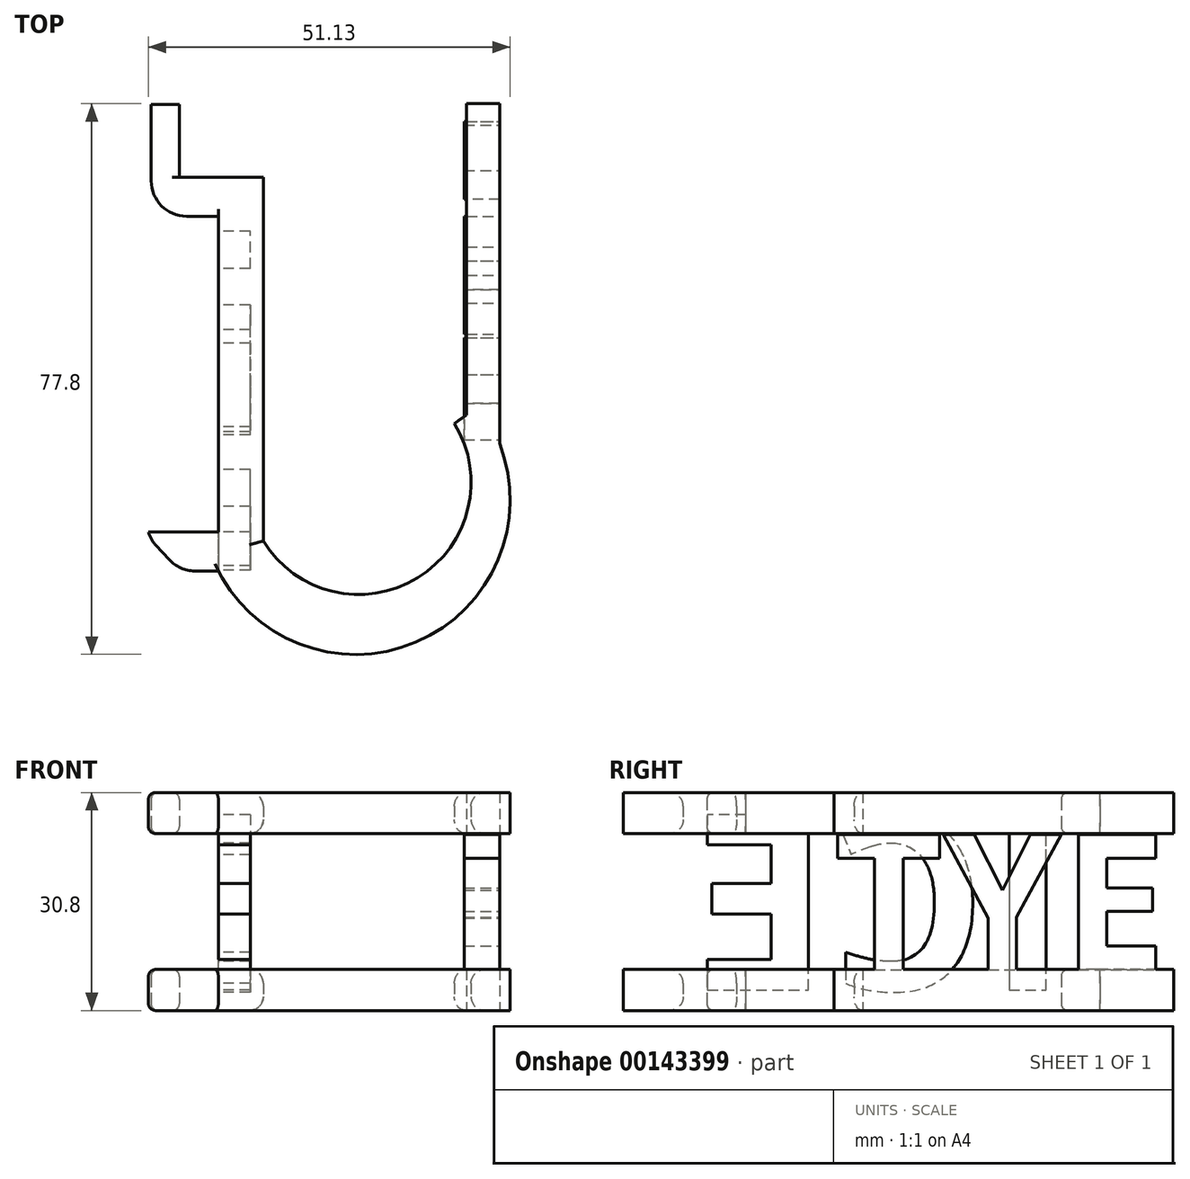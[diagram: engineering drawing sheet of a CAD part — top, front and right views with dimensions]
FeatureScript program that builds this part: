
annotation { "Feature Type Name" : "Feature", "Feature Type Description" : "" }
export const myFeature = defineFeature(function(context is Context, id is Id, definition is map)
    precondition{}
    {
        {
            var Q0;
            Q0=qCreatedBy(makeId("Top.planeOp"),FACE);
            var sketch = newSketch(context, id + "F0", { "sketchPlane" : qUnion([Q0])});
            skLineSegment(sketch, "E0.top", {"start": v(0, 55.6) * mm, "end": v(6.35, 55.6) * mm});
            skLineSegment(sketch, "E0.left", {"start": v(0, 0) * mm, "end": v(0, 55.6) * mm});
            skLineSegment(sketch, "E0.right", {"start": v(6.35, 4.23) * mm, "end": v(6.35, 55.6) * mm});
            skArc(sketch, "E1", {"start": v(0, 0) * mm, "mid": v(28.4, -9.86) * mm, "end": v(39.74, 17.98) * mm});
            skArc(sketch, "E2", {"start": v(6.35, 4.23) * mm, "mid": v(28.16, -0.98) * mm, "end": v(33.37, 20.82) * mm});
            skLineSegment(sketch, "E3", {"start": v(33.37, 20.82) * mm, "end": v(36.78, 23.26) * mm});
            skLineSegment(sketch, "E4", {"start": v(0, 55.6) * mm, "end": v(-5.5, 55.6) * mm});
            skPoint(sketch, "E5.start.orphan", {"position": v(-5.5, 50.1) * mm});
            skLineSegment(sketch, "E6", {"start": v(-5.5, 50.1) * mm, "end": v(0, 50.1) * mm});
            skLineSegment(sketch, "E7", {"start": v(0, 27.8) * mm, "end": v(33.38, 27.8) * mm, "construction": true});
            skLineSegment(sketch, "E8", {"start": v(33.38, 27.8) * mm, "end": v(-54.11, 27.8) * mm, "construction": true});
            skLineSegment(sketch, "E9.MirrorCS", {"start": v(0, 0) * mm, "end": v(-5.5, 0) * mm});
            skLineSegment(sketch, "E10.MirrorCS", {"start": v(-5.5, 5.5) * mm, "end": v(0, 5.5) * mm});
            skPoint(sketch, "E11.MirrorCS.end.orphan", {"position": v(-5.5, 5.5) * mm});
            skPoint(sketch, "E11.MirrorCS.start.orphan", {"position": v(-12.78, -1.43) * mm});
            skPoint(sketch, "E12.MirrorCS.start.orphan", {"position": v(-12.78, -7.8) * mm});
            skPoint(sketch, "E13.MirrorCS.start.orphan", {"position": v(-5.5, 0) * mm});
            skLineSegment(sketch, "E14", {"start": v(-5.5, 55.6) * mm, "end": v(-5.5, 65.91) * mm});
            skLineSegment(sketch, "E15", {"start": v(-5.5, 65.91) * mm, "end": v(-9.5, 65.91) * mm});
            skLineSegment(sketch, "E16", {"start": v(-9.5, 65.91) * mm, "end": v(-9.5, 50.1) * mm});
            skLineSegment(sketch, "E17", {"start": v(-9.5, 50.1) * mm, "end": v(-5.5, 50.1) * mm});
            skPoint(sketch, "E18.start.orphan", {"position": v(-12.78, 63.4) * mm});
            skPoint(sketch, "E19.start.orphan", {"position": v(-12.78, 57.03) * mm});
            skPoint(sketch, "E20.end.orphan", {"position": v(-26.56, 0) * mm});
            skLineSegment(sketch, "E21", {"start": v(0, 50.1) * mm, "end": v(0, 55.6) * mm, "construction": true});
            skLineSegment(sketch, "E22", {"start": v(0, 52.85) * mm, "end": v(-28.66, 52.85) * mm, "construction": true});
            skPoint(sketch, "E22.endSnap0", {"position": v(0, 52.85) * mm});
            skLineSegment(sketch, "E23", {"start": v(0, 5.5) * mm, "end": v(0, 0) * mm, "construction": true});
            skLineSegment(sketch, "E24", {"start": v(0, 2.75) * mm, "end": v(-28.66, 2.75) * mm, "construction": true});
            skLineSegment(sketch, "E25", {"start": v(-28.66, 2.75) * mm, "end": v(-28.66, 52.85) * mm, "construction": true});
            skLineSegment(sketch, "E26", {"start": v(-5.5, 5.5) * mm, "end": v(-5.5, 16.71) * mm});
            skLineSegment(sketch, "E27", {"start": v(-5.5, 16.71) * mm, "end": v(-10.12, 16.71) * mm});
            skLineSegment(sketch, "E28", {"start": v(-10.12, 16.71) * mm, "end": v(-10.12, 5) * mm});
            skLineSegment(sketch, "E29", {"start": v(-10.12, 5) * mm, "end": v(-5.5, 0) * mm});
            skLineSegment(sketch, "E30", {"start": v(35.07, 20.82) * mm, "end": v(35.07, 66) * mm});
            skPoint(sketch, "E30.startSnap0", {"position": v(35.07, 22.04) * mm});
            skLineSegment(sketch, "E31", {"start": v(39.74, 17.98) * mm, "end": v(39.74, 66) * mm});
            skLineSegment(sketch, "E32", {"start": v(39.74, 66) * mm, "end": v(35.07, 66) * mm});
            skSolve(sketch);
        }
        {
            var Q0;
            Q0=qSketchRegion(id+"F0",true);
            extrude(context, id + "F1", {"entities" : qUnion([Q0]), "depth" : 5.8 * mm});
        }
        {
            var Q0;
            Q0=makeQuery(id+"F1.opExtrude","SWEPT_EDGE",EDGE,{"disambiguationData":[OSD([sQuery(id+"F0.wireOp",EDGE,"E16"),sQuery(id+"F0.wireOp",EDGE,"E17")])]});
            fillet(context, id + "F2", {"entities" : qUnion([Q0]), "radius" : 5 * mm, "tangentPropagation" : true, "allowEdgeOverflow" : false});
        }
        {
            var Q0;
            Q0=makeQuery(id+"F1.opExtrude","SWEPT_EDGE",EDGE,{"disambiguationData":[OSD([sQuery(id+"F0.wireOp",EDGE,"E28"),sQuery(id+"F0.wireOp",EDGE,"E29")])]});
            var Q1;
            Q1=makeQuery(id+"F1.opExtrude","SWEPT_EDGE",EDGE,{"disambiguationData":[OSD([sQuery(id+"F0.wireOp",EDGE,"E9.MirrorCS"),sQuery(id+"F0.wireOp",EDGE,"E29")])]});
            fillet(context, id + "F3", {"entities" : qUnion([Q0, Q1]), "radius" : 5 * mm, "tangentPropagation" : true, "allowEdgeOverflow" : false});
        }
        {
            var Q0;
            Q0=makeQuery(id+"F1.opExtrude","CAP_EDGE",EDGE,{"disambiguationData":[OSD([sQuery(id+"F0.wireOp",EDGE,"E0.right")])],"isStart":true});
            var Q1;
            Q1=makeQuery(id+"F1.opExtrude","CAP_EDGE",EDGE,{"disambiguationData":[OSD([sQuery(id+"F0.wireOp",EDGE,"E0.right")])],"isStart":false});
            var Q2;
            Q2=makeQuery(id+"F1.opExtrude","CAP_EDGE",EDGE,{"disambiguationData":[OSD([sQuery(id+"F0.wireOp",EDGE,"E2")])],"isStart":false});
            var Q3;
            Q3=makeQuery(id+"F1.opExtrude","CAP_EDGE",EDGE,{"disambiguationData":[OSD([sQuery(id+"F0.wireOp",EDGE,"E2")])],"isStart":true});
            fillet(context, id + "F4", {"entities" : qUnion([Q0, Q1, Q2, Q3]), "radius" : 1.96 * mm, "tangentPropagation" : true, "allowEdgeOverflow" : false});
        }
        {
            var Q0;
            Q0=makeQuery(id+"F1.opExtrude","CAP_EDGE",EDGE,{"disambiguationData":[OSD([sQuery(id+"F0.wireOp",EDGE,"E26")])],"isStart":false});
            var Q1;
            Q1=makeQuery(id+"F1.opExtrude","CAP_EDGE",EDGE,{"disambiguationData":[OSD([sQuery(id+"F0.wireOp",EDGE,"E26")])],"isStart":true});
            var Q2;
            Q2=makeQuery(id+"F1.opExtrude","CAP_EDGE",EDGE,{"disambiguationData":[OSD([sQuery(id+"F0.wireOp",EDGE,"E28")])],"isStart":false});
            var Q3;
            Q3=makeQuery(id+"F1.opExtrude","CAP_EDGE",EDGE,{"disambiguationData":[OSD([sQuery(id+"F0.wireOp",EDGE,"E28")])],"isStart":true});
            var Q4;
            {var subQ0=sQuery(id+"F0.wireOp",EDGE,"E29");var subQ1=sQuery(id+"F0.wireOp",EDGE,"E28");Q4=makeQuery(id+"F3.opFillet","BLEND_EDGE",EDGE,{"blendedFrom":[makeQuery(id+"F1.opExtrude","SWEPT_EDGE",EDGE,{"disambiguationData":[OSD([subQ1,subQ0])]}),makeQuery(id+"F1.opExtrude","CAP_FACE",FACE,{"disambiguationData":[OSD([sQuery(id+"F0.wireOp",EDGE,"E0.top"),sQuery(id+"F0.wireOp",EDGE,"E0.left"),sQuery(id+"F0.wireOp",EDGE,"E0.right"),sQuery(id+"F0.wireOp",EDGE,"E1"),sQuery(id+"F0.wireOp",EDGE,"E2"),sQuery(id+"F0.wireOp",EDGE,"E3"),sQuery(id+"F0.wireOp",EDGE,"E4"),sQuery(id+"F0.wireOp",EDGE,"E6"),sQuery(id+"F0.wireOp",EDGE,"E10.MirrorCS"),sQuery(id+"F0.wireOp",EDGE,"E9.MirrorCS"),sQuery(id+"F0.wireOp",EDGE,"E14"),sQuery(id+"F0.wireOp",EDGE,"E15"),sQuery(id+"F0.wireOp",EDGE,"E16"),sQuery(id+"F0.wireOp",EDGE,"E17"),sQuery(id+"F0.wireOp",EDGE,"E26"),sQuery(id+"F0.wireOp",EDGE,"E27"),subQ1,subQ0])],"isStart":true})],"blendedInto":[makeQuery(id+"F1.opExtrude","CAP_FACE",FACE,{"disambiguationData":[OSD([sQuery(id+"F0.wireOp",EDGE,"E0.top"),sQuery(id+"F0.wireOp",EDGE,"E0.left"),sQuery(id+"F0.wireOp",EDGE,"E0.right"),sQuery(id+"F0.wireOp",EDGE,"E1"),sQuery(id+"F0.wireOp",EDGE,"E2"),sQuery(id+"F0.wireOp",EDGE,"E3"),sQuery(id+"F0.wireOp",EDGE,"E4"),sQuery(id+"F0.wireOp",EDGE,"E6"),sQuery(id+"F0.wireOp",EDGE,"E10.MirrorCS"),sQuery(id+"F0.wireOp",EDGE,"E9.MirrorCS"),sQuery(id+"F0.wireOp",EDGE,"E14"),sQuery(id+"F0.wireOp",EDGE,"E15"),sQuery(id+"F0.wireOp",EDGE,"E16"),sQuery(id+"F0.wireOp",EDGE,"E17"),sQuery(id+"F0.wireOp",EDGE,"E26"),sQuery(id+"F0.wireOp",EDGE,"E27"),subQ1,subQ0])],"isStart":true})]});}
            var Q5;
            {var subQ0=sQuery(id+"F0.wireOp",EDGE,"E29");var subQ1=sQuery(id+"F0.wireOp",EDGE,"E28");Q5=makeQuery(id+"F3.opFillet","BLEND_EDGE",EDGE,{"blendedFrom":[makeQuery(id+"F1.opExtrude","SWEPT_EDGE",EDGE,{"disambiguationData":[OSD([subQ1,subQ0])]}),makeQuery(id+"F1.opExtrude","CAP_FACE",FACE,{"disambiguationData":[OSD([sQuery(id+"F0.wireOp",EDGE,"E0.top"),sQuery(id+"F0.wireOp",EDGE,"E0.left"),sQuery(id+"F0.wireOp",EDGE,"E0.right"),sQuery(id+"F0.wireOp",EDGE,"E1"),sQuery(id+"F0.wireOp",EDGE,"E2"),sQuery(id+"F0.wireOp",EDGE,"E3"),sQuery(id+"F0.wireOp",EDGE,"E4"),sQuery(id+"F0.wireOp",EDGE,"E6"),sQuery(id+"F0.wireOp",EDGE,"E10.MirrorCS"),sQuery(id+"F0.wireOp",EDGE,"E9.MirrorCS"),sQuery(id+"F0.wireOp",EDGE,"E14"),sQuery(id+"F0.wireOp",EDGE,"E15"),sQuery(id+"F0.wireOp",EDGE,"E16"),sQuery(id+"F0.wireOp",EDGE,"E17"),sQuery(id+"F0.wireOp",EDGE,"E26"),sQuery(id+"F0.wireOp",EDGE,"E27"),subQ1,subQ0])],"isStart":false})],"blendedInto":[makeQuery(id+"F1.opExtrude","CAP_FACE",FACE,{"disambiguationData":[OSD([sQuery(id+"F0.wireOp",EDGE,"E0.top"),sQuery(id+"F0.wireOp",EDGE,"E0.left"),sQuery(id+"F0.wireOp",EDGE,"E0.right"),sQuery(id+"F0.wireOp",EDGE,"E1"),sQuery(id+"F0.wireOp",EDGE,"E2"),sQuery(id+"F0.wireOp",EDGE,"E3"),sQuery(id+"F0.wireOp",EDGE,"E4"),sQuery(id+"F0.wireOp",EDGE,"E6"),sQuery(id+"F0.wireOp",EDGE,"E10.MirrorCS"),sQuery(id+"F0.wireOp",EDGE,"E9.MirrorCS"),sQuery(id+"F0.wireOp",EDGE,"E14"),sQuery(id+"F0.wireOp",EDGE,"E15"),sQuery(id+"F0.wireOp",EDGE,"E16"),sQuery(id+"F0.wireOp",EDGE,"E17"),sQuery(id+"F0.wireOp",EDGE,"E26"),sQuery(id+"F0.wireOp",EDGE,"E27"),subQ1,subQ0])],"isStart":false})]});}
            var Q6;
            Q6=makeQuery(id+"F1.opExtrude","CAP_EDGE",EDGE,{"disambiguationData":[OSD([sQuery(id+"F0.wireOp",EDGE,"E16")])],"isStart":true});
            var Q7;
            Q7=makeQuery(id+"F1.opExtrude","CAP_EDGE",EDGE,{"disambiguationData":[OSD([sQuery(id+"F0.wireOp",EDGE,"E16")])],"isStart":false});
            var Q8;
            Q8=makeQuery(id+"F1.opExtrude","CAP_EDGE",EDGE,{"disambiguationData":[OSD([sQuery(id+"F0.wireOp",EDGE,"E14")])],"isStart":true});
            var Q9;
            Q9=makeQuery(id+"F1.opExtrude","CAP_EDGE",EDGE,{"disambiguationData":[OSD([sQuery(id+"F0.wireOp",EDGE,"E14")])],"isStart":false});
            fillet(context, id + "F5", {"entities" : qUnion([Q0, Q1, Q2, Q3, Q4, Q5, Q6, Q7, Q8, Q9]), "radius" : 1 * mm, "tangentPropagation" : true, "allowEdgeOverflow" : false});
        }
        {
            var Q0;
            Q0=makeQuery(id+"F1.opExtrude","CAP_FACE",FACE,{"disambiguationData":[OSD([sQuery(id+"F0.wireOp",EDGE,"E0.top"),sQuery(id+"F0.wireOp",EDGE,"E0.left"),sQuery(id+"F0.wireOp",EDGE,"E0.right"),sQuery(id+"F0.wireOp",EDGE,"E1"),sQuery(id+"F0.wireOp",EDGE,"E2"),sQuery(id+"F0.wireOp",EDGE,"E3"),sQuery(id+"F0.wireOp",EDGE,"E4"),sQuery(id+"F0.wireOp",EDGE,"E6"),sQuery(id+"F0.wireOp",EDGE,"E10.MirrorCS"),sQuery(id+"F0.wireOp",EDGE,"E9.MirrorCS"),sQuery(id+"F0.wireOp",EDGE,"E14"),sQuery(id+"F0.wireOp",EDGE,"E15"),sQuery(id+"F0.wireOp",EDGE,"E16"),sQuery(id+"F0.wireOp",EDGE,"E17"),sQuery(id+"F0.wireOp",EDGE,"E26"),sQuery(id+"F0.wireOp",EDGE,"E27"),sQuery(id+"F0.wireOp",EDGE,"E28"),sQuery(id+"F0.wireOp",EDGE,"E29")])],"isStart":false});
            var sketch = newSketch(context, id + "F6", { "sketchPlane" : qUnion([Q0])});
            skLineSegment(sketch, "E33.bottom", {"start": v(-5.38, 5.5) * mm, "end": v(-13.14, 5.5) * mm});
            skLineSegment(sketch, "E33.top", {"start": v(-5.38, 17.8) * mm, "end": v(-13.14, 17.8) * mm});
            skLineSegment(sketch, "E33.left", {"start": v(-5.38, 5.5) * mm, "end": v(-5.38, 17.8) * mm});
            skLineSegment(sketch, "E33.right", {"start": v(-13.14, 5.5) * mm, "end": v(-13.14, 17.8) * mm});
            skSolve(sketch);
        }
        {
            var Q0;
            Q0=makeQuery(id+"F6.imprint","IMPRINT",FACE,{"disambiguationData":[TD([[makeQuery(id+"F6.imprint","IMPRINT",EDGE,{"derivedFrom":sQuery(id+"F6.wireOp",EDGE,"E33.top")}),1.0]])]});
            var Q1;
            {var subQ2=sQuery(id+"F0.wireOp",EDGE,"E27");Q1=makeQuery(id+"F6.imprint","IMPRINT",FACE,{"disambiguationData":[TD([[makeQuery(id+"F6.imprint","IMPRINT",EDGE,{"derivedFrom":makeQuery(id+"F1.opExtrude","CAP_EDGE",EDGE,{"disambiguationData":[OSD([subQ2])],"isStart":false})}),1.0]])]});}
            extrude(context, id + "F7", {"entities" : qUnion([Q0, Q1]), "operationType" : NewBodyOperationType.REMOVE, "endBound" : BoundingType.THROUGH_ALL, "oppositeDirection" : true, "depth" : 25 * mm, "hasSecondDirection" : true, "secondDirectionOppositeDirection" : false, "secondDirectionDepth" : 25 * mm});
        }
        {
            var Q0;
            Q0=makeQuery(id+"F1.opExtrude","SWEPT_BODY",BODY,{"disambiguationData":[OSD([sQuery(id+"F0.wireOp",EDGE,"E0.top"),sQuery(id+"F0.wireOp",EDGE,"E0.left"),sQuery(id+"F0.wireOp",EDGE,"E0.right"),sQuery(id+"F0.wireOp",EDGE,"E1"),sQuery(id+"F0.wireOp",EDGE,"E2"),sQuery(id+"F0.wireOp",EDGE,"E3"),sQuery(id+"F0.wireOp",EDGE,"E4"),sQuery(id+"F0.wireOp",EDGE,"E6"),sQuery(id+"F0.wireOp",EDGE,"E10.MirrorCS"),sQuery(id+"F0.wireOp",EDGE,"E9.MirrorCS"),sQuery(id+"F0.wireOp",EDGE,"E14"),sQuery(id+"F0.wireOp",EDGE,"E15"),sQuery(id+"F0.wireOp",EDGE,"E16"),sQuery(id+"F0.wireOp",EDGE,"E17"),sQuery(id+"F0.wireOp",EDGE,"E26"),sQuery(id+"F0.wireOp",EDGE,"E27"),sQuery(id+"F0.wireOp",EDGE,"E28"),sQuery(id+"F0.wireOp",EDGE,"E29")])]});
            transform(context, id + "F8", {"entities" : qUnion([Q0]), "transformType" : TransformType.TRANSLATION_3D, "dx" : 0 * mm, "dy" : 0 * mm, "dz" : 25 * mm, "makeCopy" : true});
        }
        {
            var Q0;
            Q0=makeQuery(id+"F8.opPattern","COPY",FACE,{"derivedFrom":makeQuery(id+"F1.opExtrude","SWEPT_FACE",FACE,{"disambiguationData":[OSD([sQuery(id+"F0.wireOp",EDGE,"E0.left")])]}),"instanceName":"1"});
            var sketch = newSketch(context, id + "F9", { "sketchPlane" : qUnion([Q0])});
            skLineSegment(sketch, "E34.bottom", {"start": v(0, 0) * mm, "end": v(-51.1, 0) * mm, "construction": true});
            skLineSegment(sketch, "E34.top", {"start": v(0, 30.8) * mm, "end": v(-51.1, 30.8) * mm, "construction": true});
            skLineSegment(sketch, "E34.left", {"start": v(0, 0) * mm, "end": v(0, 30.8) * mm, "construction": true});
            skLineSegment(sketch, "E34.right", {"start": v(-51.1, 0) * mm, "end": v(-51.1, 30.8) * mm, "construction": true});
            skLineSegment(sketch, "E35.bottom", {"start": v(-51.1, 30.8) * mm, "end": v(-5.5, 30.8) * mm, "construction": true});
            skLineSegment(sketch, "E35.top", {"start": v(-51.1, 25) * mm, "end": v(-5.5, 25) * mm, "construction": true});
            skLineSegment(sketch, "E35.left", {"start": v(-51.1, 30.8) * mm, "end": v(-51.1, 25) * mm, "construction": true});
            skLineSegment(sketch, "E35.right", {"start": v(-5.5, 30.8) * mm, "end": v(-5.5, 25) * mm, "construction": true});
            skLineSegment(sketch, "E36.bottom", {"start": v(-51.1, 27.9) * mm, "end": v(86.07, 27.9) * mm, "construction": true});
            skLineSegment(sketch, "E36.top", {"start": v(-51.1, 2.9) * mm, "end": v(86.07, 2.9) * mm, "construction": true});
            skLineSegment(sketch, "E36.left", {"start": v(-51.1, 27.9) * mm, "end": v(-51.1, 2.9) * mm, "construction": true});
            skLineSegment(sketch, "E36.right", {"start": v(86.07, 27.9) * mm, "end": v(86.07, 2.9) * mm, "construction": true});
            skText(sketch, "E37", { "text": "ICEMAN", "fontName": "OpenSans-Bold.ttf"});
            const initialGuessF9  = {"E37": [-0.0511, 0.0029, 1, 0, 0.025]};
            skSetInitialGuess(sketch, initialGuessF9);
            skSolve(sketch);
        }
        {
            var Q0;
            {var subQ0=sQuery(id+"F9.wireOp",EDGE,"E37.sketch_text.stroke-3");Q0=makeQuery(id+"F9.imprint","IMPRINT",FACE,{"disambiguationData":[TD([[makeQuery(id+"F9.imprint","IMPRINT",EDGE,{"derivedFrom":subQ0}),-1.0]])]});}
            var Q1;
            Q1=makeQuery(id+"F9.imprint","IMPRINT",FACE,{"disambiguationData":[TD([[makeQuery(id+"F9.imprint","IMPRINT",EDGE,{"derivedFrom":sQuery(id+"F9.wireOp",EDGE,"E37.sketch_text.stroke-4")}),-1.0]])]});
            var Q2;
            {var subQ8=sQuery(id+"F9.wireOp",EDGE,"E37.sketch_text.stroke-19");Q2=makeQuery(id+"F9.imprint","IMPRINT",FACE,{"disambiguationData":[TD([[makeQuery(id+"F9.imprint","IMPRINT",EDGE,{"derivedFrom":subQ8}),-1.0]])]});}
            extrude(context, id + "F10", {"entities" : qUnion([Q0, Q1, Q2]), "oppositeDirection" : true, "depth" : 4.5 * mm});
        }
        {
            var Q0;
            Q0=makeQuery(id+"F8.opPattern","COPY",FACE,{"derivedFrom":makeQuery(id+"F1.opExtrude","SWEPT_FACE",FACE,{"disambiguationData":[OSD([sQuery(id+"F0.wireOp",EDGE,"E31")])]}),"instanceName":"1"});
            var sketch = newSketch(context, id + "F11", { "sketchPlane" : qUnion([Q0])});
            skText(sketch, "E38", { "text": "TYE", "fontName": "OpenSans-Bold.ttf"});
            const initialGuessF11  = {"E38": [0.01798, 0.00578, 1, 0, 0.01922]};
            skSetInitialGuess(sketch, initialGuessF11);
            skSolve(sketch);
        }
        {
            var Q0;
            Q0 = qSketchRegion(id + "F11", true);
            extrude(context, id + "F12", {"entities" : qUnion([Q0]), "operationType" : NewBodyOperationType.ADD, "oppositeDirection" : true, "depth" : 5 * mm});
        }
    });
